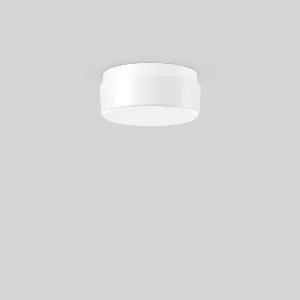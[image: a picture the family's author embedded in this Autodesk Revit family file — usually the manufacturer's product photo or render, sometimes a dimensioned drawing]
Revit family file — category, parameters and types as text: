
# Revit family: kreis_21171_002_b27d
name_source: partatom
category: Lighting Fixtures
units: mm (PartAtom-declared; Revit-internal decimal feet)

## family parameters
Cut with Voids When Loaded = No
Host = Face
Light Source = No
Part Type = Normal
Room Calculation Point = No
Round Connector Dimension = Use Diameter
Shared = No

## types (1)
- KREIS (1 x QA60/clear E27, 1320 lm, 77 W, 3000)
    Apparent Load = 77 VA
    CIE Flux Codes = 34 63 85 71 62
    Color Rendering = 90
    Color Temperature = 3000
    Default Elevation = 1800 mm
    Description = Series: KREIS
Round surface-mounted luminaire in classic design. Base: plastic. Opal glass: mouth-blown, satin finish. Diffuser fastening: spring system. Suitable for Ceiling mounting, Wall (surface). IP 43 ceiling mounting, IP 44 wall mounting. 
Colour: white
Diameter: 280 mm
Height: 120 mm
Lamp: A60
Number of lamps: 1
Wattage: 100 W
Socket: E27
System power: 75 W
Rated luminous flux: 590 lm
Luminous efficiency: 8 lm/W
Control gear: Converter not necessary
Protection class: II
Type of protection: IP 43
    Height = 120 mm
    Lamp = 1 x QA60/clear E27
    Lamp Light Flux = 1320 lm
    Lamp Power = 77 W
    Lamp count = 1
    Length = 280 mm
    Lifetime = 3000 h
    Luminous efficacy = 11 lm/W
    Manufacturer = RZB
    ModVariant = No
    Model = 21171.002
    Mounting Place = Ceiling, Wall
    Mounting Type = Surface mounted
    Number of Poles = 1
    OnlyDefault = Yes
    Power Factor = 1
    Product Name = KREIS
    Product group = Surface mounted ceiling and wall luminaires
    ProductGroupID = 305
    Protection Class = Protection class II
    Protection Degree = IP 43
    RLX_Detail_Level = 1
    RLX_Emergency_Light_Flux = 0 lm
    RLX_Emergency_Type = 0
    RLX_Emergency_Type_DB = No
    RlxData = <blob elided: 11601 chars, md5=79751952>
    Socket = E27
    Standby Power = 0 W
    System Light Flux = 815 lm
    System Power = 77 W
    Type Comments = Product without accessories
    Type Image = 21171.002.jpg
    URL = http://relux.com
    VarID = ---
    Voltage = 230 V
    Voltage Range = 220-240 V
    Weight = 0.00 kg
    Width = 0 mm  [stored 0 ft]

note: [stored X ft] marks values corroborated as IEEE doubles in the binary element streams (Revit-internal decimal feet)

## geometry (parser evidence)
native form markers: Sweep x14
no freeform markers — native parametric forms only
